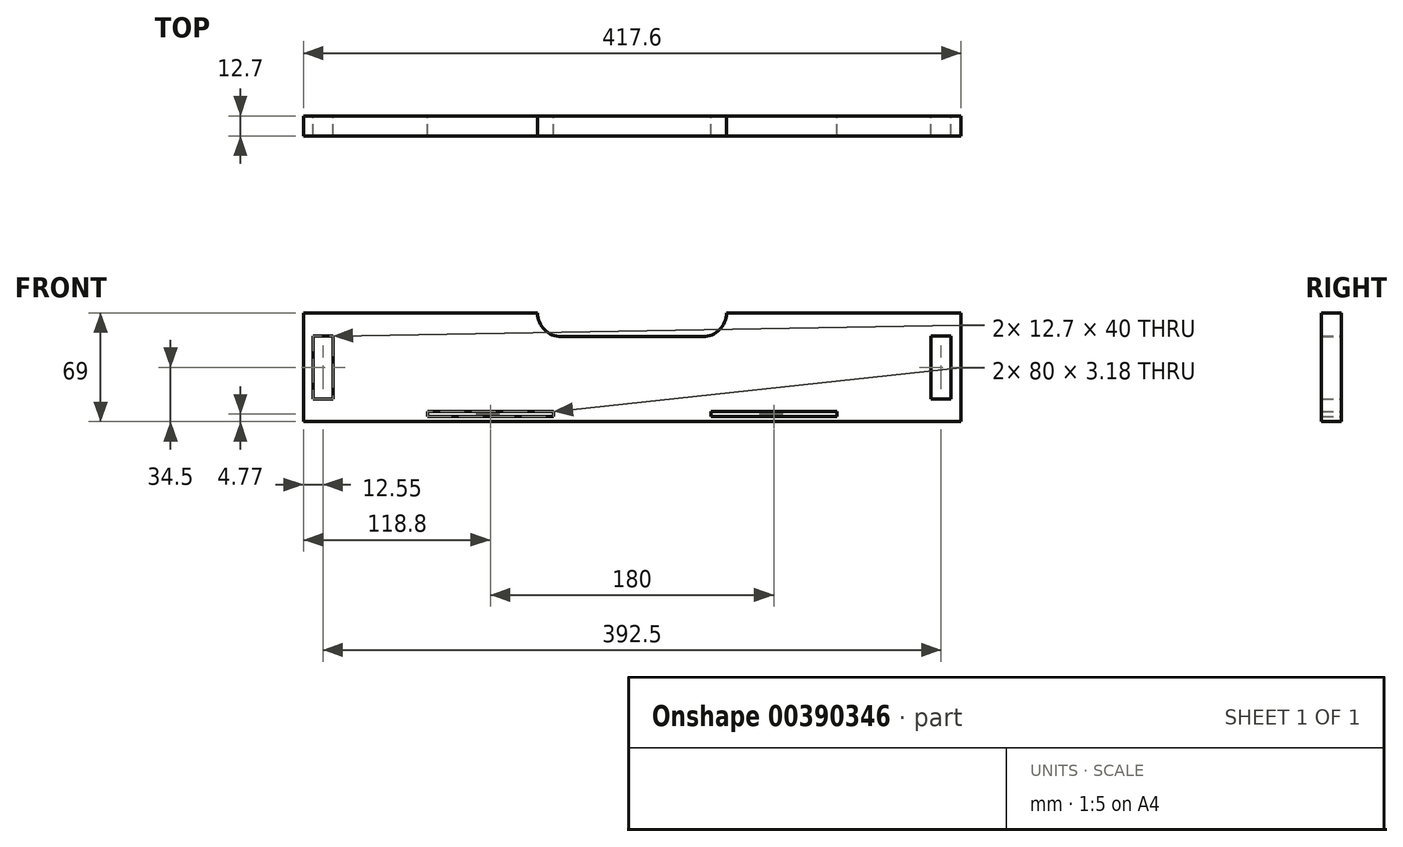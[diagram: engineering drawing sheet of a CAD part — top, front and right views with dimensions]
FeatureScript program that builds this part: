
annotation { "Feature Type Name" : "Feature", "Feature Type Description" : "" }
export const myFeature = defineFeature(function(context is Context, id is Id, definition is map)
    precondition{}
    {
        {
            assignVariable(context, id + "F0", {"name" : "MW", "anyValue" : 12.7});
        }
        {
            var Q0;
            Q0=qCreatedBy(makeId("Front.planeOp"),FACE);
            var sketch = newSketch(context, id + "F1", { "sketchPlane" : qUnion([Q0])});
            skLineSegment(sketch, "E0.bottom", {"start": v(-208.8, -3.18) * mm, "end": v(208.8, -3.18) * mm});
            skLineSegment(sketch, "E0.top", {"start": v(-208.8, 65.82) * mm, "end": v(-60, 65.82) * mm});
            skLineSegment(sketch, "E0.left", {"start": v(-208.8, -3.18) * mm, "end": v(-208.8, 65.82) * mm});
            skLineSegment(sketch, "E0.right", {"start": v(208.8, -3.18) * mm, "end": v(208.8, 65.82) * mm});
            skPoint(sketch, "E0.middle", {"position": v(0, 31.32) * mm});
            skLineSegment(sketch, "E1", {"start": v(0, 31.32) * mm, "end": v(-208.8, 31.32) * mm, "construction": true});
            skLineSegment(sketch, "E2.bottom", {"start": v(-189.9, 11.32) * mm, "end": v(-202.6, 11.32) * mm});
            skLineSegment(sketch, "E2.top", {"start": v(-189.9, 51.32) * mm, "end": v(-202.6, 51.32) * mm});
            skLineSegment(sketch, "E2.left", {"start": v(-189.9, 11.32) * mm, "end": v(-189.9, 51.32) * mm});
            skLineSegment(sketch, "E2.right", {"start": v(-202.6, 11.32) * mm, "end": v(-202.6, 51.32) * mm});
            skPoint(sketch, "E2.middle", {"position": v(-196.25, 31.32) * mm});
            skLineSegment(sketch, "E3.MirrorCS", {"start": v(189.9, 51.32) * mm, "end": v(202.6, 51.32) * mm});
            skLineSegment(sketch, "E4.MirrorCS", {"start": v(189.9, 11.32) * mm, "end": v(189.9, 51.32) * mm});
            skLineSegment(sketch, "E5.MirrorCS", {"start": v(189.9, 11.32) * mm, "end": v(202.6, 11.32) * mm});
            skLineSegment(sketch, "E6.MirrorCS", {"start": v(202.6, 11.32) * mm, "end": v(202.6, 51.32) * mm});
            skPoint(sketch, "E7.MirrorP", {"position": v(196.25, 31.32) * mm});
            skLineSegment(sketch, "E8.bottom", {"start": v(-50, 0) * mm, "end": v(-130, 0) * mm});
            skLineSegment(sketch, "E8.top", {"start": v(-50, 3.18) * mm, "end": v(-130, 3.18) * mm});
            skLineSegment(sketch, "E8.left", {"start": v(-50, 0) * mm, "end": v(-50, 3.18) * mm});
            skLineSegment(sketch, "E8.right", {"start": v(-130, 0) * mm, "end": v(-130, 3.18) * mm});
            skPoint(sketch, "E8.middle", {"position": v(-90, 1.6) * mm});
            skLineSegment(sketch, "E9.MirrorCS", {"start": v(130, 0) * mm, "end": v(130, 3.18) * mm});
            skLineSegment(sketch, "E10.MirrorCS", {"start": v(50, 0) * mm, "end": v(50, 3.18) * mm});
            skPoint(sketch, "E11.MirrorP", {"position": v(90, 1.6) * mm});
            skLineSegment(sketch, "E12.MirrorCS", {"start": v(50, 3.18) * mm, "end": v(130, 3.18) * mm});
            skLineSegment(sketch, "E13.MirrorCS", {"start": v(50, 0) * mm, "end": v(130, 0) * mm});
            skLineSegment(sketch, "E14.top", {"start": v(-45, 50.82) * mm, "end": v(45, 50.82) * mm});
            skLineSegment(sketch, "E14.left", {"start": v(-60, 65.82) * mm, "end": v(-60, 65.82) * mm});
            skLineSegment(sketch, "E14.right", {"start": v(60, 65.82) * mm, "end": v(60, 65.82) * mm});
            skPoint(sketch, "E14.middle", {"position": v(0, 58.32) * mm});
            skLineSegment(sketch, "E15.trimOffspring", {"start": v(60, 65.82) * mm, "end": v(208.8, 65.82) * mm});
            skPoint(sketch, "E16.visualSharp", {"position": v(-60, 50.82) * mm});
            skArc(sketch, "E16.filletArc", {"start": v(-60, 65.82) * mm, "mid": v(-55.6, 55.21) * mm, "end": v(-45, 50.82) * mm});
            skPoint(sketch, "E17.visualSharp", {"position": v(60, 50.82) * mm});
            skArc(sketch, "E17.filletArc", {"start": v(45, 50.82) * mm, "mid": v(55.6, 55.21) * mm, "end": v(60, 65.82) * mm});
            skSolve(sketch);
        }
        {
            var Q0;
            Q0 = qSketchRegion(id + "F1", true);
            extrude(context, id + "F2", {"entities" : qUnion([Q0]), "depth" : (getVariable(context, 'MW')) * mm});
        }
    });
